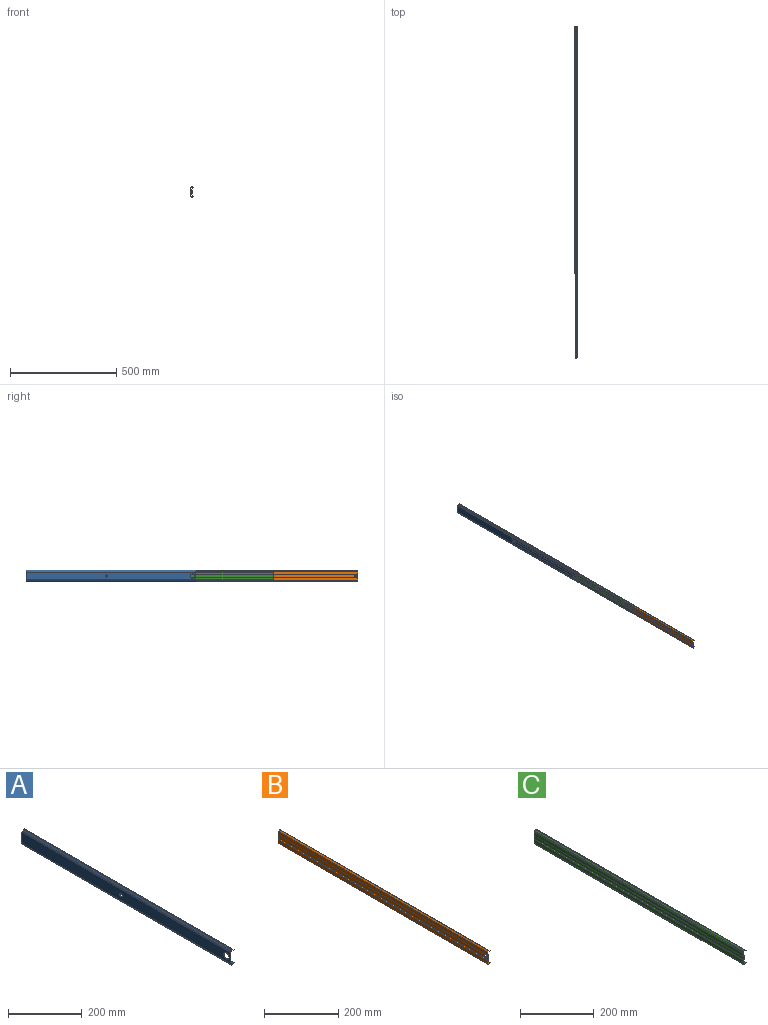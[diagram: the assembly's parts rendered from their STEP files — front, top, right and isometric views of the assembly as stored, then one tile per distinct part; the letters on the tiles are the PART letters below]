
ASSEMBLY  parts=3 mates=2
PART A: 24 faces, bbox 14x800x52.4 mm
  f0: plane 800x35.86mm, normal (1,0,0), area 28293.6mm2, adj f16,f17,f20,f21,f22,f23
  f1: plane 800x3.54mm, normal (0.71,0,-0.71), area 4000mm2, adj f2,f16,f17,f21
  f2: plane 800x2mm, normal (0,0,-1), area 1600mm2, adj f1,f3,f16,f17
  f3: plane 800x5mm, normal (-0.71,0,-0.71), area 5656.9mm2, adj f2,f4,f16,f17
  f4: plane 800x0.85mm, normal (0.71,0,-0.71), area 960mm2, adj f3,f5,f16,f17
  f5: plane 800x5.35mm, normal (0.71,0,0.71), area 6054.5mm2, adj f4,f6,f16,f17
  f6: plane 800x2.99mm, normal (0,0,1), area 2395.3mm2, adj f5,f7,f16,f17
  f7: plane 800x4.24mm, normal (-0.71,0,0.71), area 4795.3mm2, adj f6,f16,f17,f18
  f8: plane 800x36.85mm, normal (-1,0,0), area 29088.9mm2, adj f16,f17,f18,f19,f22,f23
  f9: plane 800x4.24mm, normal (-0.71,0,-0.71), area 4795.3mm2, adj f10,f16,f17,f19
  f10: plane 800x2.99mm, normal (0,0,-1), area 2395.3mm2, adj f9,f11,f16,f17
  f11: plane 800x5.35mm, normal (0.71,0,-0.71), area 6054.5mm2, adj f10,f12,f16,f17
  f12: plane 800x0.85mm, normal (0.71,0,0.71), area 960mm2, adj f11,f13,f16,f17
  f13: plane 800x5mm, normal (-0.71,0,0.71), area 5656.9mm2, adj f12,f14,f16,f17
  f14: plane 800x2mm, normal (0,0,1), area 1600mm2, adj f13,f15,f16,f17
  f15: plane 800x3.54mm, normal (0.71,0,0.71), area 4000mm2, adj f14,f16,f17,f20
  f16: plane 52.4x14.05mm, normal (0,-1,0), area 90.3mm2, adj f0,f1,f2,f3,f4,f5,f6,f7
  f17: plane 52.4x14.05mm, normal (0,1,0), area 90.3mm2, adj f0,f1,f2,f3,f4,f5,f6,f7
  f18: cylinder r=5mm len=800mm, axis (0,1,0), area 3141.6mm2, adj f7,f8,f16,f17
  f19: cylinder r=5mm len=800mm, axis (0,-1,0), area 3141.6mm2, adj f8,f9,f16,f17
  f20: cylinder r=5mm len=800mm, axis (0,1,0), area 3141.6mm2, adj f0,f15,f16,f17
  f21: cylinder r=5mm len=800mm, axis (0,-1,0), area 3141.6mm2, adj f0,f1,f16,f17
  f22: cylinder r=10mm len=20mm, axis (-1,0,0), area 75.4mm2, adj f0,f8
  f23: cylinder r=5mm len=10mm, axis (-1,0,0), area 37.7mm2, adj f0,f8
PART B: 27 faces, bbox 10x800x47.6 mm
  f0: plane 800x4.3mm, normal (-0.71,0,-0.71), area 4861.6mm2, adj f1,f23,f24,f25
  f1: plane 800x1.01mm, normal (0,0,-1), area 804.7mm2, adj f0,f2,f24,f25
  f2: plane 800x4.65mm, normal (0.71,0,-0.71), area 5259.2mm2, adj f1,f3,f24,f25
  f3: plane 800x0.85mm, normal (0.71,0,0.71), area 960mm2, adj f2,f4,f24,f25
  f4: plane 800x4.3mm, normal (-0.71,0,0.71), area 4861.6mm2, adj f3,f5,f24,f25
  f5: plane 800x0.01mm, normal (0,0,1), area 9.4mm2, adj f4,f6,f24,f25
  f6: plane 800x3.59mm, normal (0.71,0,0.71), area 4066.3mm2, adj f5,f7,f24,f25
  f7: plane 800x10.31mm, normal (1,0,0), area 8244.7mm2, adj f6,f8,f24,f25
  f8: plane 800x3.8mm, normal (0,0,-1), area 3040mm2, adj f7,f9,f24,f25
  f9: plane 800x17.4mm, normal (1,0,0), area 13841.5mm2, adj f8,f10,f24,f25,f26
  f10: plane 800x3.8mm, normal (0,0,1), area 3040mm2, adj f9,f11,f24,f25
  f11: plane 800x10.31mm, normal (1,0,0), area 8244.7mm2, adj f10,f12,f24,f25
  f12: plane 800x3.59mm, normal (0.71,0,-0.71), area 4066.3mm2, adj f11,f13,f24,f25
  f13: plane 800x0.01mm, normal (0,0,-1), area 9.4mm2, adj f12,f14,f24,f25
  f14: plane 800x4.3mm, normal (-0.71,0,-0.71), area 4861.6mm2, adj f13,f15,f24,f25
  f15: plane 800x0.85mm, normal (0.71,0,-0.71), area 960mm2, adj f14,f16,f24,f25
  f16: plane 800x4.65mm, normal (0.71,0,0.71), area 5259.2mm2, adj f15,f17,f24,f25
  f17: plane 800x1.01mm, normal (0,0,1), area 804.7mm2, adj f16,f18,f24,f25
  f18: plane 800x4.3mm, normal (-0.71,0,0.71), area 4861.6mm2, adj f17,f19,f24,f25
  f19: plane 800x12mm, normal (-1,0,0), area 9602.4mm2, adj f18,f20,f24,f25
  f20: plane 800x3.8mm, normal (0,0,-1), area 3040mm2, adj f19,f21,f24,f25
  f21: plane 800x15mm, normal (-1,0,0), area 11921.5mm2, adj f20,f22,f24,f25,f26
  f22: plane 800x3.8mm, normal (0,0,1), area 3040mm2, adj f21,f23,f24,f25
  f23: plane 800x12mm, normal (-1,0,0), area 9602.4mm2, adj f0,f22,f24,f25
  f24: plane 47.6x9.95mm, normal (0,-1,0), area 85.1mm2, adj f0,f1,f2,f3,f4,f5,f6,f7
  f25: plane 47.6x9.95mm, normal (0,1,0), area 85.1mm2, adj f0,f1,f2,f3,f4,f5,f6,f7
  f26: cylinder r=5mm len=10mm, axis (-1,0,0), area 37.7mm2, adj f9,f21
PART C: 28 faces, bbox 12x800x50 mm
  f0: plane 800x4.3mm, normal (0.71,0,0.71), area 4861.6mm2, adj f1,f23,f24,f25
  f1: plane 800x12mm, normal (1,0,0), area 9602.4mm2, adj f0,f2,f24,f25
  f2: plane 800x3.8mm, normal (0,0,-1), area 3040mm2, adj f1,f3,f24,f25
  f3: plane 800x15mm, normal (1,0,0), area 12000mm2, adj f2,f4,f24,f25
  f4: plane 800x3.8mm, normal (0,0,1), area 3040mm2, adj f3,f5,f24,f25
  f5: plane 800x12mm, normal (1,0,0), area 9602.4mm2, adj f4,f6,f24,f25
  f6: plane 800x4.3mm, normal (0.71,0,-0.71), area 4861.6mm2, adj f5,f7,f24,f25
  f7: plane 800x1.01mm, normal (0,0,-1), area 804.7mm2, adj f6,f8,f24,f25
  f8: plane 800x4.65mm, normal (-0.71,0,-0.71), area 5259.2mm2, adj f7,f9,f24,f25
  f9: plane 800x0.85mm, normal (0.71,0,-0.71), area 960mm2, adj f8,f10,f24,f25
  f10: plane 800x5mm, normal (0.71,0,0.71), area 5656.9mm2, adj f9,f11,f24,f25
  f11: plane 800x2mm, normal (0,0,1), area 1600mm2, adj f10,f12,f24,f25
  f12: plane 800x3.54mm, normal (-0.71,0,0.71), area 4000mm2, adj f11,f24,f25,f26
  f13: plane 800x11.63mm, normal (-1,0,0), area 9303.1mm2, adj f14,f24,f25,f26
  f14: plane 800x3.8mm, normal (0,0,-1), area 3040mm2, adj f13,f15,f24,f25
  f15: plane 800x12.6mm, normal (-1,0,0), area 10080mm2, adj f14,f16,f24,f25
  f16: plane 800x3.8mm, normal (0,0,1), area 3040mm2, adj f15,f17,f24,f25
  f17: plane 800x11.63mm, normal (-1,0,0), area 9303.1mm2, adj f16,f24,f25,f27
  f18: plane 800x3.54mm, normal (-0.71,0,-0.71), area 4000mm2, adj f19,f24,f25,f27
  f19: plane 800x2mm, normal (0,0,-1), area 1600mm2, adj f18,f20,f24,f25
  f20: plane 800x5mm, normal (0.71,0,-0.71), area 5656.9mm2, adj f19,f21,f24,f25
  f21: plane 800x0.85mm, normal (0.71,0,0.71), area 960mm2, adj f20,f22,f24,f25
  f22: plane 800x4.65mm, normal (-0.71,0,0.71), area 5259.2mm2, adj f21,f23,f24,f25
  f23: plane 800x1.01mm, normal (0,0,1), area 804.7mm2, adj f0,f22,f24,f25
  f24: plane 50x12mm, normal (0,-1,0), area 91.2mm2, adj f0,f1,f2,f3,f4,f5,f6,f7
  f25: plane 50x12mm, normal (0,1,0), area 91.2mm2, adj f0,f1,f2,f3,f4,f5,f6,f7
  f26: cylinder r=5mm len=800mm, axis (0,1,0), area 3141.6mm2, adj f12,f13,f24,f25
  f27: cylinder r=5mm len=800mm, axis (0,1,0), area 3141.6mm2, adj f17,f18,f24,f25
PLACE A t=(188.77,99.76,-66.72)mm fixed
PLACE B t=(192.8,-665.19,-68.26)mm
PLACE C t=(188.77,-265.54,-66.72)mm
MATE slider C.f24 <-> B.f24  axis (0,1,0) through (189.97,-1065.54,-86.22)mm
MATE slider A.f16 <-> C.f24  axis (0,1,0) through (190.23,-700.24,-88.19)mm
